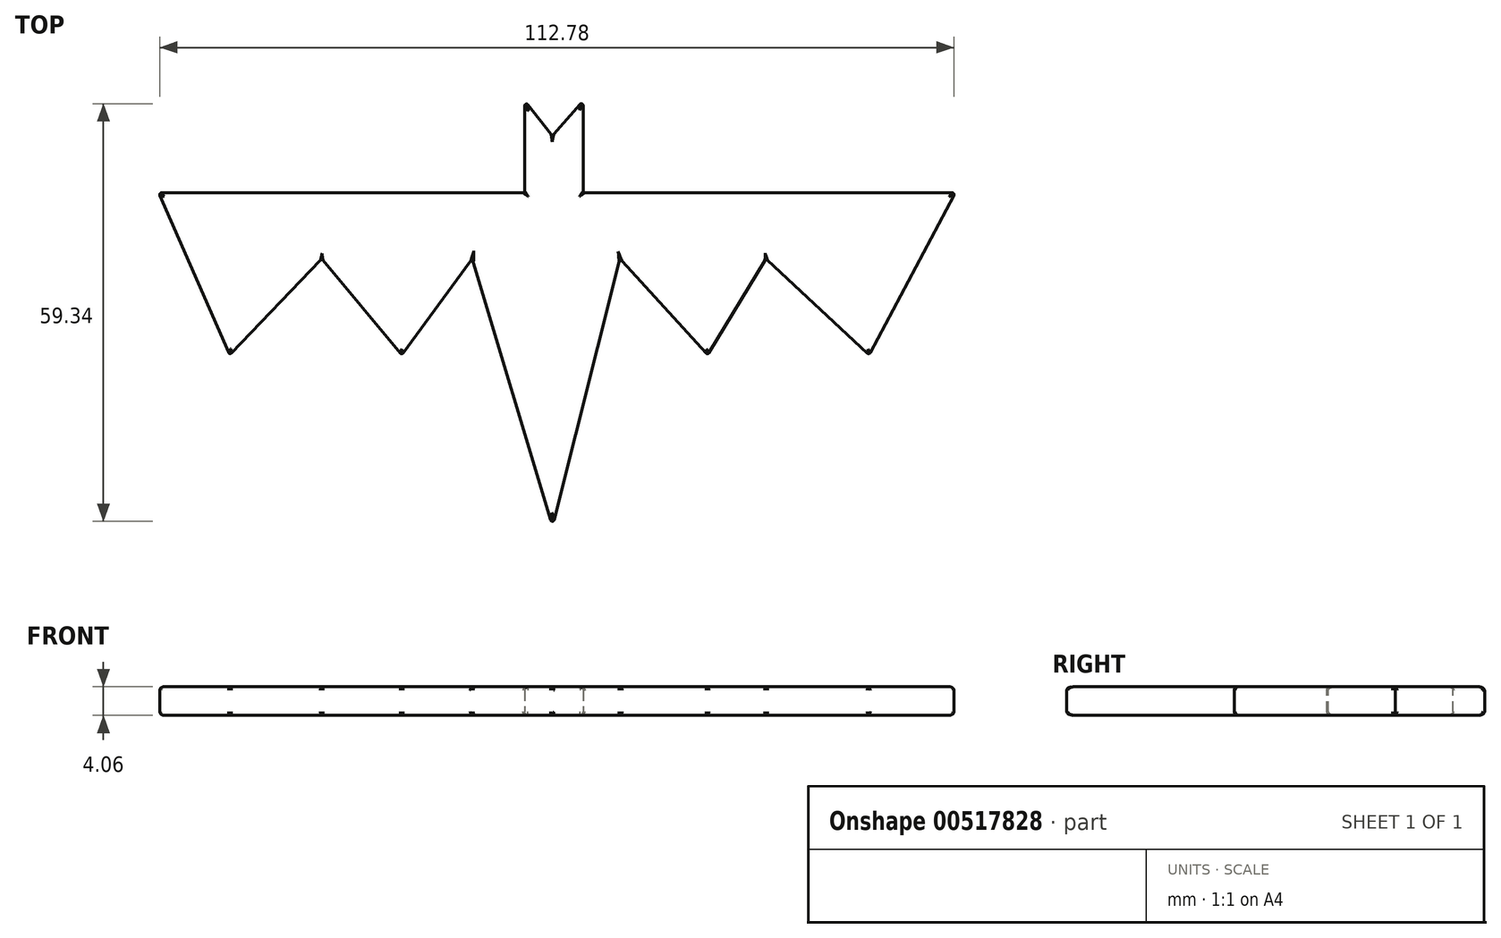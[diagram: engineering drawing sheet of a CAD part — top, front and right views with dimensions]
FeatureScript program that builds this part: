
annotation { "Feature Type Name" : "Feature", "Feature Type Description" : "" }
export const myFeature = defineFeature(function(context is Context, id is Id, definition is map)
    precondition{}
    {
        {
            var Q0;
            Q0=qCreatedBy(makeId("Top.planeOp"),FACE);
            var sketch = newSketch(context, id + "F0", { "sketchPlane" : qUnion([Q0])});
            skLineSegment(sketch, "E0", {"start": v(-55.89, 23.03) * mm, "end": v(-3.93, 23.03) * mm});
            skLineSegment(sketch, "E1", {"start": v(-3.93, 23.03) * mm, "end": v(-3.93, 36.13) * mm});
            skLineSegment(sketch, "E2", {"start": v(-3.93, 36.13) * mm, "end": v(0, 31.1) * mm});
            skLineSegment(sketch, "E3", {"start": v(0, 31.1) * mm, "end": v(4.37, 36.13) * mm});
            skLineSegment(sketch, "E4", {"start": v(4.37, 36.13) * mm, "end": v(4.37, 23.03) * mm});
            skLineSegment(sketch, "E5", {"start": v(4.37, 23.03) * mm, "end": v(57.2, 23.03) * mm});
            skLineSegment(sketch, "E6", {"start": v(57.2, 23.03) * mm, "end": v(44.97, 0) * mm});
            skLineSegment(sketch, "E7", {"start": v(44.97, 0) * mm, "end": v(30.34, 13.64) * mm});
            skLineSegment(sketch, "E8", {"start": v(30.34, 13.64) * mm, "end": v(22.05, 0) * mm});
            skLineSegment(sketch, "E9", {"start": v(22.05, 0) * mm, "end": v(9.6, 13.64) * mm});
            skLineSegment(sketch, "E10", {"start": v(9.6, 13.64) * mm, "end": v(0, -24.34) * mm});
            skLineSegment(sketch, "E11", {"start": v(0, -24.34) * mm, "end": v(-11.35, 13.64) * mm});
            skLineSegment(sketch, "E12", {"start": v(-11.35, 13.64) * mm, "end": v(-21.4, 0) * mm});
            skLineSegment(sketch, "E13", {"start": v(-21.4, 0) * mm, "end": v(-32.75, 13.64) * mm});
            skLineSegment(sketch, "E14", {"start": v(-32.75, 13.64) * mm, "end": v(-45.84, 0) * mm});
            skLineSegment(sketch, "E15", {"start": v(-45.84, 0) * mm, "end": v(-55.89, 23.03) * mm});
            skSolve(sketch);
        }
        {
            var Q0;
            Q0=makeQuery(id+"F0.imprint","IMPRINT",FACE,{"disambiguationData":[TD([[makeQuery(id+"F0.imprint","IMPRINT",EDGE,{"derivedFrom":sQuery(id+"F0.wireOp",EDGE,"E0")}),-1.0]])]});
            extrude(context, id + "F1", {"entities" : qUnion([Q0]), "depth" : 4.06 * mm, "offsetDistance" : 25.4 * mm});
        }
        {
            var Q0;
            Q0=makeQuery(id+"F1.opExtrude","CAP_FACE",FACE,{"disambiguationData":[OSD([sQuery(id+"F0.wireOp",EDGE,"E0"),sQuery(id+"F0.wireOp",EDGE,"E1"),sQuery(id+"F0.wireOp",EDGE,"E2"),sQuery(id+"F0.wireOp",EDGE,"E3"),sQuery(id+"F0.wireOp",EDGE,"E4"),sQuery(id+"F0.wireOp",EDGE,"E5"),sQuery(id+"F0.wireOp",EDGE,"E6"),sQuery(id+"F0.wireOp",EDGE,"E7"),sQuery(id+"F0.wireOp",EDGE,"E8"),sQuery(id+"F0.wireOp",EDGE,"E9"),sQuery(id+"F0.wireOp",EDGE,"E10"),sQuery(id+"F0.wireOp",EDGE,"E11"),sQuery(id+"F0.wireOp",EDGE,"E12"),sQuery(id+"F0.wireOp",EDGE,"E13"),sQuery(id+"F0.wireOp",EDGE,"E14"),sQuery(id+"F0.wireOp",EDGE,"E15")])],"isStart":false});
            var Q1;
            Q1=makeQuery(id+"F1.opExtrude","CAP_FACE",FACE,{"disambiguationData":[OSD([sQuery(id+"F0.wireOp",EDGE,"E0"),sQuery(id+"F0.wireOp",EDGE,"E1"),sQuery(id+"F0.wireOp",EDGE,"E2"),sQuery(id+"F0.wireOp",EDGE,"E3"),sQuery(id+"F0.wireOp",EDGE,"E4"),sQuery(id+"F0.wireOp",EDGE,"E5"),sQuery(id+"F0.wireOp",EDGE,"E6"),sQuery(id+"F0.wireOp",EDGE,"E7"),sQuery(id+"F0.wireOp",EDGE,"E8"),sQuery(id+"F0.wireOp",EDGE,"E9"),sQuery(id+"F0.wireOp",EDGE,"E10"),sQuery(id+"F0.wireOp",EDGE,"E11"),sQuery(id+"F0.wireOp",EDGE,"E12"),sQuery(id+"F0.wireOp",EDGE,"E13"),sQuery(id+"F0.wireOp",EDGE,"E14"),sQuery(id+"F0.wireOp",EDGE,"E15")])],"isStart":true});
            fillet(context, id + "F2", {"entities" : qUnion([Q0, Q1]), "radius" : 0.5 * mm, "tangentPropagation" : true, "allowEdgeOverflow" : false});
        }
        {
            var Q0;
            Q0=makeQuery(id+"F1.opExtrude","SWEPT_EDGE",EDGE,{"disambiguationData":[OSD([sQuery(id+"F0.wireOp",EDGE,"E1"),sQuery(id+"F0.wireOp",EDGE,"E2")])]});
            var Q1;
            Q1=makeQuery(id+"F1.opExtrude","SWEPT_EDGE",EDGE,{"disambiguationData":[OSD([sQuery(id+"F0.wireOp",EDGE,"E3"),sQuery(id+"F0.wireOp",EDGE,"E4")])]});
            var Q2;
            Q2=makeQuery(id+"F1.opExtrude","SWEPT_EDGE",EDGE,{"disambiguationData":[OSD([sQuery(id+"F0.wireOp",EDGE,"E2"),sQuery(id+"F0.wireOp",EDGE,"E3")])]});
            var Q3;
            Q3=makeQuery(id+"F1.opExtrude","SWEPT_EDGE",EDGE,{"disambiguationData":[OSD([sQuery(id+"F0.wireOp",EDGE,"E0"),sQuery(id+"F0.wireOp",EDGE,"E1")])]});
            var Q4;
            Q4=makeQuery(id+"F1.opExtrude","SWEPT_EDGE",EDGE,{"disambiguationData":[OSD([sQuery(id+"F0.wireOp",EDGE,"E4"),sQuery(id+"F0.wireOp",EDGE,"E5")])]});
            var Q5;
            Q5=makeQuery(id+"F1.opExtrude","SWEPT_EDGE",EDGE,{"disambiguationData":[OSD([sQuery(id+"F0.wireOp",EDGE,"E5"),sQuery(id+"F0.wireOp",EDGE,"E6")])]});
            var Q6;
            Q6=makeQuery(id+"F1.opExtrude","SWEPT_EDGE",EDGE,{"disambiguationData":[OSD([sQuery(id+"F0.wireOp",EDGE,"E6"),sQuery(id+"F0.wireOp",EDGE,"E7")])]});
            var Q7;
            Q7=makeQuery(id+"F1.opExtrude","SWEPT_EDGE",EDGE,{"disambiguationData":[OSD([sQuery(id+"F0.wireOp",EDGE,"E8"),sQuery(id+"F0.wireOp",EDGE,"E9")])]});
            var Q8;
            Q8=makeQuery(id+"F1.opExtrude","SWEPT_EDGE",EDGE,{"disambiguationData":[OSD([sQuery(id+"F0.wireOp",EDGE,"E12"),sQuery(id+"F0.wireOp",EDGE,"E13")])]});
            var Q9;
            Q9=makeQuery(id+"F1.opExtrude","SWEPT_EDGE",EDGE,{"disambiguationData":[OSD([sQuery(id+"F0.wireOp",EDGE,"E14"),sQuery(id+"F0.wireOp",EDGE,"E15")])]});
            var Q10;
            Q10=makeQuery(id+"F1.opExtrude","SWEPT_EDGE",EDGE,{"disambiguationData":[OSD([sQuery(id+"F0.wireOp",EDGE,"E7"),sQuery(id+"F0.wireOp",EDGE,"E8")])]});
            var Q11;
            Q11=makeQuery(id+"F1.opExtrude","SWEPT_EDGE",EDGE,{"disambiguationData":[OSD([sQuery(id+"F0.wireOp",EDGE,"E9"),sQuery(id+"F0.wireOp",EDGE,"E10")])]});
            var Q12;
            Q12=makeQuery(id+"F1.opExtrude","SWEPT_EDGE",EDGE,{"disambiguationData":[OSD([sQuery(id+"F0.wireOp",EDGE,"E10"),sQuery(id+"F0.wireOp",EDGE,"E11")])]});
            var Q13;
            Q13=makeQuery(id+"F1.opExtrude","SWEPT_EDGE",EDGE,{"disambiguationData":[OSD([sQuery(id+"F0.wireOp",EDGE,"E11"),sQuery(id+"F0.wireOp",EDGE,"E12")])]});
            var Q14;
            Q14=makeQuery(id+"F1.opExtrude","SWEPT_EDGE",EDGE,{"disambiguationData":[OSD([sQuery(id+"F0.wireOp",EDGE,"E13"),sQuery(id+"F0.wireOp",EDGE,"E14")])]});
            var Q15;
            Q15=makeQuery(id+"F1.opExtrude","SWEPT_EDGE",EDGE,{"disambiguationData":[OSD([sQuery(id+"F0.wireOp",EDGE,"E0"),sQuery(id+"F0.wireOp",EDGE,"E15")])]});
            fillet(context, id + "F3", {"entities" : qUnion([Q0, Q1, Q2, Q3, Q4, Q5, Q6, Q7, Q8, Q9, Q10, Q11, Q12, Q13, Q14, Q15]), "radius" : 0.25 * mm, "tangentPropagation" : true, "allowEdgeOverflow" : false});
        }
    });
